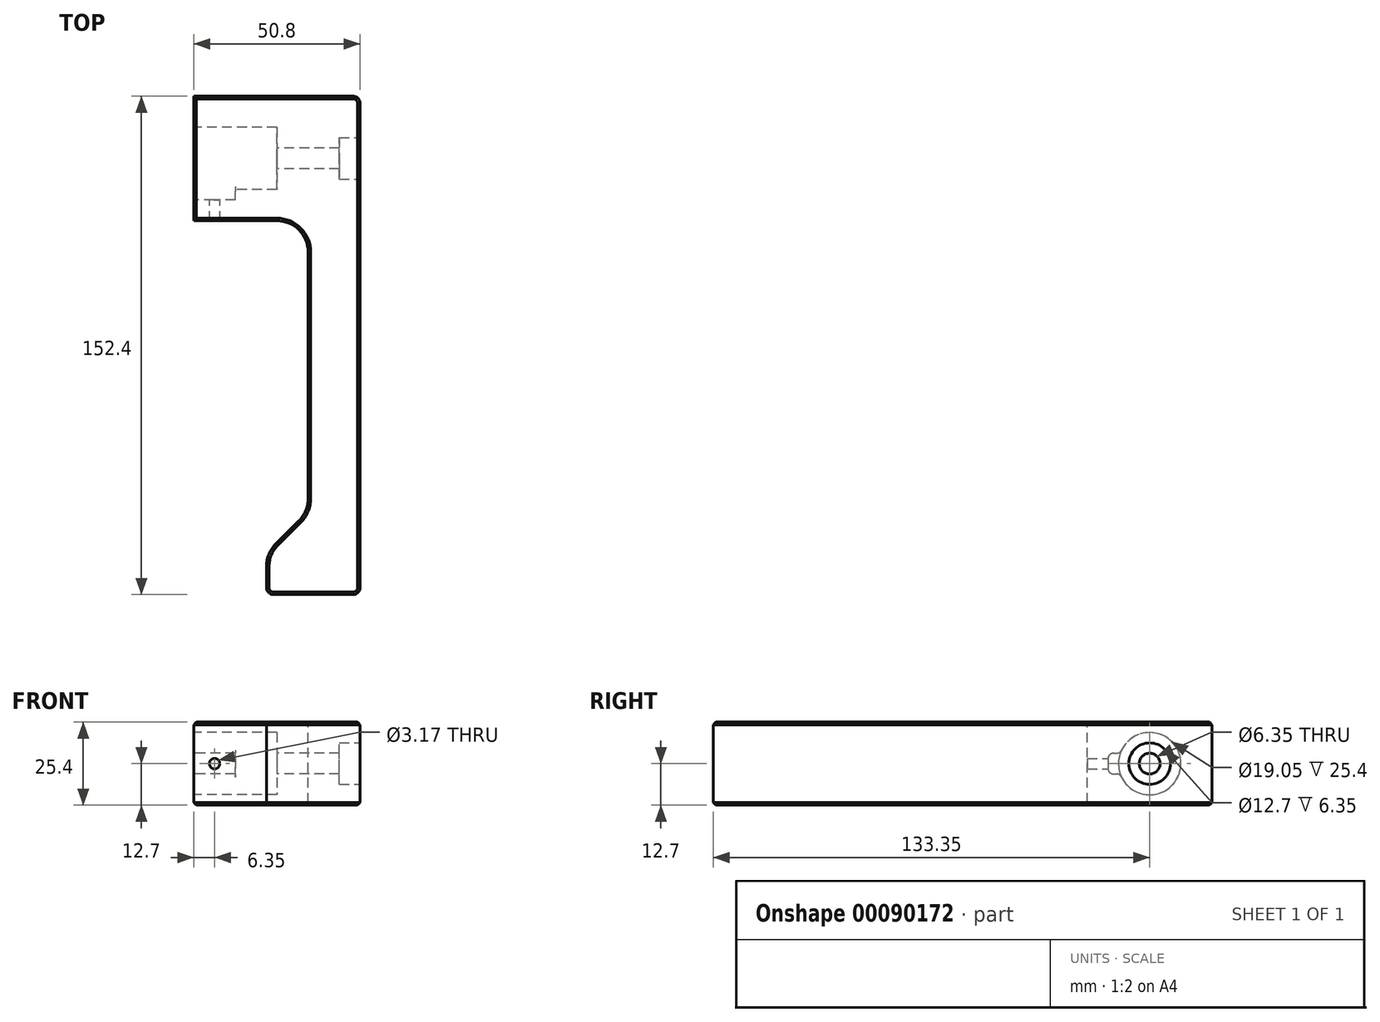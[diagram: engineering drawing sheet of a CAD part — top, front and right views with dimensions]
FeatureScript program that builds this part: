
annotation { "Feature Type Name" : "Feature", "Feature Type Description" : "" }
export const myFeature = defineFeature(function(context is Context, id is Id, definition is map)
    precondition{}
    {
        {
            var Q0;
            Q0=qCreatedBy(makeId("Top.planeOp"),FACE);
            var sketch = newSketch(context, id + "F0", { "sketchPlane" : qUnion([Q0])});
            skPoint(sketch, "E0.endSnap0", {"position": v(0, 76.2) * mm});
            skLineSegment(sketch, "E1", {"start": v(0, 38.1) * mm, "end": v(-25.4, 38.1) * mm});
            skLineSegment(sketch, "E2", {"start": v(0, 38.1) * mm, "end": v(0, 38.1) * mm});
            skLineSegment(sketch, "E3", {"start": v(9.53, 28.58) * mm, "end": v(9.53, -46.85) * mm});
            skLineSegment(sketch, "E4", {"start": v(9.53, -76.2) * mm, "end": v(-1.1, -76.2) * mm});
            skLineSegment(sketch, "E5", {"start": v(-3.17, -74.12) * mm, "end": v(-3.17, -67.45) * mm});
            skLineSegment(sketch, "E6", {"start": v(-0.39, -60.71) * mm, "end": v(6.74, -53.59) * mm});
            skPoint(sketch, "E7.visualSharp", {"position": v(9.53, 38.1) * mm});
            skArc(sketch, "E7.filletArc", {"start": v(9.53, 28.58) * mm, "mid": v(6.74, 35.31) * mm, "end": v(0, 38.1) * mm});
            skPoint(sketch, "E8.visualSharp", {"position": v(-3.17, -63.5) * mm});
            skArc(sketch, "E8.filletArc", {"start": v(-0.39, -60.71) * mm, "mid": v(-2.45, -63.8) * mm, "end": v(-3.17, -67.45) * mm});
            skPoint(sketch, "E9.visualSharp", {"position": v(-3.17, -76.2) * mm});
            skArc(sketch, "E9.filletArc", {"start": v(-3.17, -74.12) * mm, "mid": v(-2.57, -75.6) * mm, "end": v(-1.1, -76.2) * mm});
            skLineSegment(sketch, "E10", {"start": v(9.53, -76.2) * mm, "end": v(23.32, -76.2) * mm});
            skLineSegment(sketch, "E11", {"start": v(25.4, -74.12) * mm, "end": v(25.4, 74.12) * mm});
            skLineSegment(sketch, "E12", {"start": v(23.32, 76.2) * mm, "end": v(-25.4, 76.2) * mm});
            skLineSegment(sketch, "E13", {"start": v(-25.4, 76.2) * mm, "end": v(-25.4, 38.1) * mm});
            skPoint(sketch, "E14.visualSharp", {"position": v(25.4, -76.2) * mm});
            skArc(sketch, "E14.filletArc", {"start": v(23.32, -76.2) * mm, "mid": v(24.8, -75.6) * mm, "end": v(25.4, -74.12) * mm});
            skPoint(sketch, "E15.visualSharp", {"position": v(25.4, 76.2) * mm});
            skArc(sketch, "E15.filletArc", {"start": v(25.4, 74.12) * mm, "mid": v(24.8, 75.6) * mm, "end": v(23.32, 76.2) * mm});
            skPoint(sketch, "E16.visualSharp", {"position": v(9.53, -50.8) * mm});
            skArc(sketch, "E16.filletArc", {"start": v(6.74, -53.59) * mm, "mid": v(8.8, -50.5) * mm, "end": v(9.53, -46.85) * mm});
            skSolve(sketch);
        }
        {
            var Q0;
            Q0=makeQuery(id+"F0.imprint","IMPRINT",FACE,{"disambiguationData":[TD([[makeQuery(id+"F0.imprint","IMPRINT",EDGE,{"derivedFrom":sQuery(id+"F0.wireOp",EDGE,"E1")}),1.0]])]});
            var Q1;
            Q1=makeQuery(id+"F0.imprint","IMPRINT",FACE,{"disambiguationData":[TD([[makeQuery(id+"F0.imprint","IMPRINT",EDGE,{"derivedFrom":sQuery(id+"F0.wireOp",EDGE,"E1")}),-1.0]])]});
            extrude(context, id + "F1", {"entities" : qUnion([Q0, Q1]), "endBound" : BoundingType.SYMMETRIC, "oppositeDirection" : true, "depth" : 25.4 * mm});
        }
        {
            var Q0;
            Q0=makeQuery(id+"F1.opExtrude","SWEPT_FACE",FACE,{"disambiguationData":[OSD([sQuery(id+"F0.wireOp",EDGE,"E13")])]});
            var sketch = newSketch(context, id + "F2", { "sketchPlane" : qUnion([Q0])});
            skArc(sketch, "E17", {"start": v(-48.55, 4.09) * mm, "mid": v(-66.68, 0) * mm, "end": v(-48.55, -4.09) * mm});
            skLineSegment(sketch, "E18.bottom", {"start": v(-46.05, 3.17) * mm, "end": v(-47.1, 3.17) * mm});
            skLineSegment(sketch, "E18.top", {"start": v(-46.05, -3.18) * mm, "end": v(-47.1, -3.18) * mm});
            skLineSegment(sketch, "E18.left", {"start": v(-44.45, 1.57) * mm, "end": v(-44.45, -1.57) * mm});
            skPoint(sketch, "E18.middle", {"position": v(-47.63, 0) * mm});
            skPoint(sketch, "E19.orphan", {"position": v(-50.8, 3.17) * mm});
            skPoint(sketch, "E20.orphan", {"position": v(-50.8, -3.18) * mm});
            skPoint(sketch, "E21.visualSharp", {"position": v(-48.17, 3.17) * mm});
            skArc(sketch, "E21.filletArc", {"start": v(-48.55, 4.09) * mm, "mid": v(-47.96, 3.42) * mm, "end": v(-47.1, 3.17) * mm});
            skPoint(sketch, "E22.visualSharp", {"position": v(-48.17, -3.18) * mm});
            skArc(sketch, "E22.filletArc", {"start": v(-47.1, -3.18) * mm, "mid": v(-47.96, -3.42) * mm, "end": v(-48.55, -4.09) * mm});
            skPoint(sketch, "E23.visualSharp", {"position": v(-44.45, -3.18) * mm});
            skArc(sketch, "E23.filletArc", {"start": v(-46.05, -3.18) * mm, "mid": v(-44.92, -2.7) * mm, "end": v(-44.45, -1.57) * mm});
            skPoint(sketch, "E24.visualSharp", {"position": v(-44.45, 3.17) * mm});
            skArc(sketch, "E24.filletArc", {"start": v(-44.45, 1.57) * mm, "mid": v(-44.92, 2.7) * mm, "end": v(-46.05, 3.17) * mm});
            skArc(sketch, "E25", {"start": v(-48.55, -4.09) * mm, "mid": v(-47.63, 0) * mm, "end": v(-48.55, 4.09) * mm});
            skSolve(sketch);
        }
        {
            var Q0;
            {var subQ0=sQuery(id+"F2.wireOp",EDGE,"E25");var subQ1=makeQuery(id+"F2.imprint","INTERSECT",VERTEX,{"derivedFrom":[sQuery(id+"F2.wireOp",EDGE,"E21.filletArc"),subQ0]});Q0=makeQuery(id+"F2.imprint","IMPRINT",FACE,{"disambiguationData":[TD([[makeQuery(id+"F2.imprint","IMPRINT",EDGE,{"disambiguationData":[TD([[subQ1,-1.0]])],"derivedFrom":subQ0}),1.0]])]});}
            extrude(context, id + "F3", {"entities" : qUnion([Q0]), "operationType" : NewBodyOperationType.REMOVE, "oppositeDirection" : true, "depth" : 25.4 * mm});
        }
        {
            var Q0;
            Q0=makeQuery(id+"F3.boolean.opBoolean","COPY",FACE,{"derivedFrom":makeQuery(id+"F3.opExtrude","CAP_FACE",FACE,{"disambiguationData":[OSD([sQuery(id+"F2.wireOp",EDGE,"E25")])],"isStart":false})});
            var sketch = newSketch(context, id + "F4", { "sketchPlane" : qUnion([Q0])});
            skCircle(sketch, "E26", {"center": v(-57.15, 0) * mm, "radius": 3.18 * mm});
            skSolve(sketch);
        }
        {
            var Q0;
            Q0 = qSketchRegion(id + "F4", true);
            extrude(context, id + "F5", {"entities" : qUnion([Q0]), "operationType" : NewBodyOperationType.REMOVE, "oppositeDirection" : true, "depth" : 25.4 * mm});
        }
        {
            var Q0;
            Q0=makeQuery(id+"F1.opExtrude","SWEPT_FACE",FACE,{"disambiguationData":[OSD([sQuery(id+"F0.wireOp",EDGE,"E11")])]});
            var sketch = newSketch(context, id + "F6", { "sketchPlane" : qUnion([Q0])});
            skCircle(sketch, "E27", {"center": v(57.15, 0) * mm, "radius": 6.35 * mm});
            skSolve(sketch);
        }
        {
            var Q0;
            Q0 = qSketchRegion(id + "F6", true);
            extrude(context, id + "F7", {"entities" : qUnion([Q0]), "operationType" : NewBodyOperationType.REMOVE, "oppositeDirection" : true, "depth" : 6.35 * mm});
        }
        {
            var Q0;
            Q0=makeQuery(id+"F1.opExtrude","CAP_FACE",FACE,{"disambiguationData":[OSD([sQuery(id+"F0.wireOp",EDGE,"E1"),sQuery(id+"F0.wireOp",EDGE,"E3"),sQuery(id+"F0.wireOp",EDGE,"E4"),sQuery(id+"F0.wireOp",EDGE,"E5"),sQuery(id+"F0.wireOp",EDGE,"E6"),sQuery(id+"F0.wireOp",EDGE,"E7.filletArc"),sQuery(id+"F0.wireOp",EDGE,"E8.filletArc"),sQuery(id+"F0.wireOp",EDGE,"E9.filletArc"),sQuery(id+"F0.wireOp",EDGE,"E10"),sQuery(id+"F0.wireOp",EDGE,"E11"),sQuery(id+"F0.wireOp",EDGE,"E12"),sQuery(id+"F0.wireOp",EDGE,"E13"),sQuery(id+"F0.wireOp",EDGE,"E14.filletArc"),sQuery(id+"F0.wireOp",EDGE,"E15.filletArc")])],"isStart":true});
            var Q1;
            Q1=makeQuery(id+"F1.opExtrude","CAP_FACE",FACE,{"disambiguationData":[OSD([sQuery(id+"F0.wireOp",EDGE,"E1"),sQuery(id+"F0.wireOp",EDGE,"E3"),sQuery(id+"F0.wireOp",EDGE,"E4"),sQuery(id+"F0.wireOp",EDGE,"E5"),sQuery(id+"F0.wireOp",EDGE,"E6"),sQuery(id+"F0.wireOp",EDGE,"E7.filletArc"),sQuery(id+"F0.wireOp",EDGE,"E8.filletArc"),sQuery(id+"F0.wireOp",EDGE,"E9.filletArc"),sQuery(id+"F0.wireOp",EDGE,"E10"),sQuery(id+"F0.wireOp",EDGE,"E11"),sQuery(id+"F0.wireOp",EDGE,"E12"),sQuery(id+"F0.wireOp",EDGE,"E13"),sQuery(id+"F0.wireOp",EDGE,"E14.filletArc"),sQuery(id+"F0.wireOp",EDGE,"E15.filletArc")])],"isStart":false});
            var Q2;
            Q2=makeQuery(id+"F7.boolean.opBoolean","COPY",EDGE,{"derivedFrom":makeQuery(id+"F7.opExtrude","CAP_EDGE",EDGE,{"disambiguationData":[OSD([sQuery(id+"F6.wireOp",EDGE,"E27")])],"isStart":true})});
            chamfer(context, id + "F8", {"entities" : qUnion([Q0, Q1, Q2]), "width" : 0.8 * mm, "tangentPropagation" : true});
        }
        {
            var Q0;
            Q0=makeQuery(id+"F2.imprint","IMPRINT",FACE,{"disambiguationData":[TD([[makeQuery(id+"F2.imprint","IMPRINT",EDGE,{"derivedFrom":sQuery(id+"F2.wireOp",EDGE,"E18.bottom")}),1.0]])]});
            extrude(context, id + "F9", {"entities" : qUnion([Q0]), "operationType" : NewBodyOperationType.REMOVE, "oppositeDirection" : true, "depth" : 12.7 * mm});
        }
        {
            var Q0;
            Q0=makeQuery(id+"F9.boolean.opBoolean","COPY",FACE,{"derivedFrom":makeQuery(id+"F9.opExtrude","SWEPT_FACE",FACE,{"disambiguationData":[OSD([sQuery(id+"F2.wireOp",EDGE,"E18.left")])]})});
            var sketch = newSketch(context, id + "F10", { "sketchPlane" : qUnion([Q0])});
            skCircle(sketch, "E28", {"center": v(19.05, 0) * mm, "radius": 1.59 * mm});
            skPoint(sketch, "E28.centerSnap0", {"position": v(19.05, 1.57) * mm});
            skPoint(sketch, "E28.centerSnap1", {"position": v(12.7, 0) * mm});
            skSolve(sketch);
        }
        {
            var Q0;
            Q0 = qSketchRegion(id + "F10", true);
            extrude(context, id + "F11", {"entities" : qUnion([Q0]), "operationType" : NewBodyOperationType.REMOVE, "oppositeDirection" : true, "depth" : 25.4 * mm});
        }
    });
